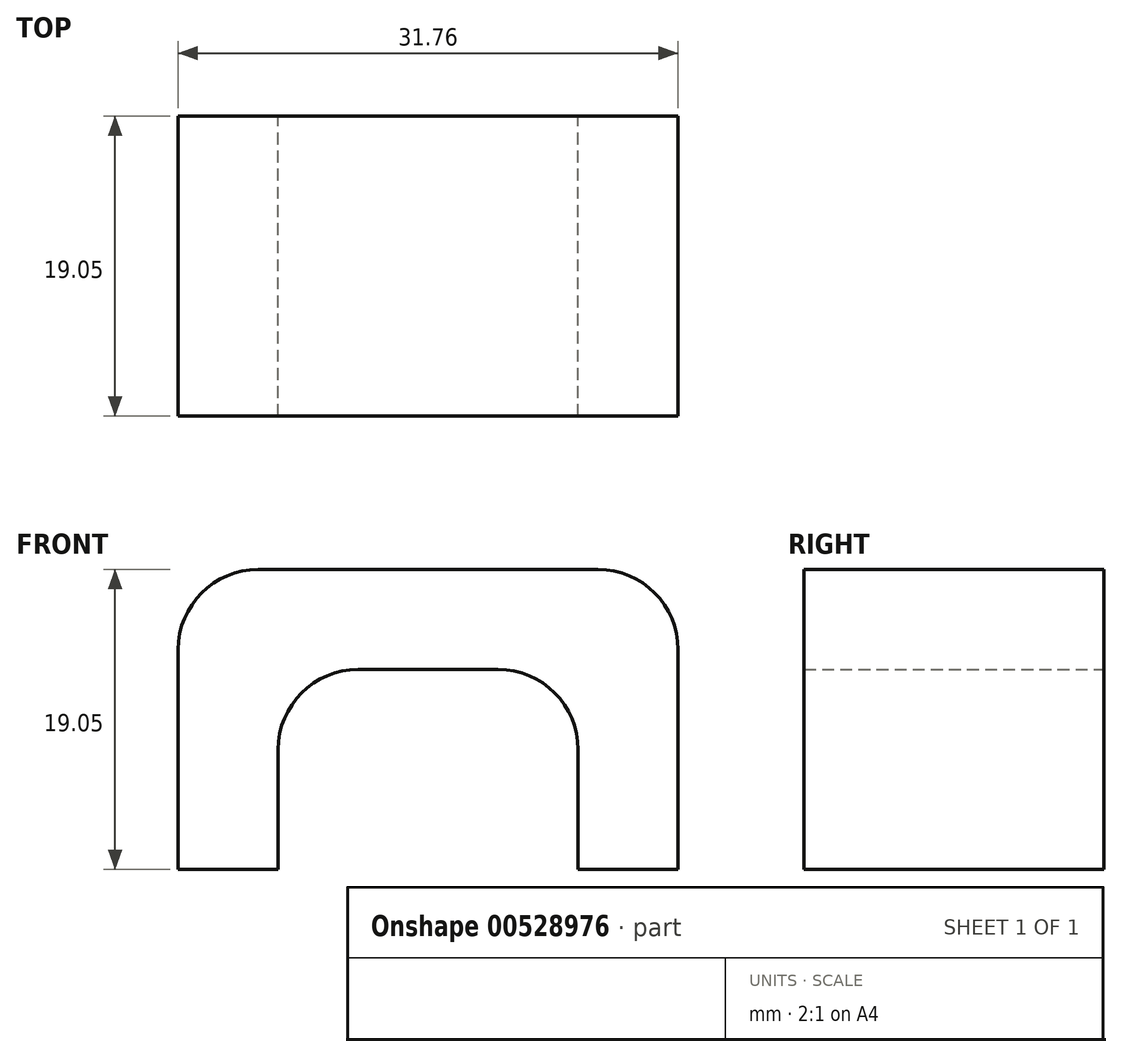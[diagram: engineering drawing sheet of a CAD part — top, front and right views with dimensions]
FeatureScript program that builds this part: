
annotation { "Feature Type Name" : "Feature", "Feature Type Description" : "" }
export const myFeature = defineFeature(function(context is Context, id is Id, definition is map)
    precondition{}
    {
        {
            var Q0;
            Q0=qCreatedBy(makeId("Front.planeOp"),FACE);
            var sketch = newSketch(context, id + "F0", { "sketchPlane" : qUnion([Q0])});
            skLineSegment(sketch, "E0", {"start": v(0, 0) * mm, "end": v(-15.87, 0) * mm});
            skLineSegment(sketch, "E1", {"start": v(-15.87, 0) * mm, "end": v(-15.87, -19.05) * mm});
            skLineSegment(sketch, "E2", {"start": v(-15.87, -19.05) * mm, "end": v(-9.52, -19.05) * mm});
            skLineSegment(sketch, "E3", {"start": v(-9.52, -19.05) * mm, "end": v(-9.52, -6.35) * mm});
            skLineSegment(sketch, "E4", {"start": v(-9.52, -6.35) * mm, "end": v(0, -6.35) * mm});
            skLineSegment(sketch, "E5", {"start": v(0, -6.35) * mm, "end": v(0, 0) * mm, "construction": true});
            skLineSegment(sketch, "E6.MirrorCS", {"start": v(15.88, 0) * mm, "end": v(15.88, -19.05) * mm});
            skLineSegment(sketch, "E7.MirrorCS", {"start": v(15.87, -19.05) * mm, "end": v(9.52, -19.05) * mm});
            skLineSegment(sketch, "E8.MirrorCS", {"start": v(9.52, -19.05) * mm, "end": v(9.52, -6.35) * mm});
            skLineSegment(sketch, "E9.MirrorCS", {"start": v(0, 0) * mm, "end": v(15.87, 0) * mm});
            skLineSegment(sketch, "E10.MirrorCS", {"start": v(9.52, -6.35) * mm, "end": v(0, -6.35) * mm});
            skSolve(sketch);
        }
        {
            var Q0;
            Q0=qSketchRegion(id+"F0",true);
            extrude(context, id + "F1", {"entities" : qUnion([Q0]), "depth" : 19.05 * mm});
        }
        {
            var Q0;
            Q0=makeQuery(id+"F1.opExtrude","SWEPT_EDGE",EDGE,{"disambiguationData":[OSD([sQuery(id+"F0.wireOp",EDGE,"E0"),sQuery(id+"F0.wireOp",EDGE,"E1")])]});
            var Q1;
            Q1=makeQuery(id+"F1.opExtrude","SWEPT_EDGE",EDGE,{"disambiguationData":[OSD([sQuery(id+"F0.wireOp",EDGE,"E3"),sQuery(id+"F0.wireOp",EDGE,"E4")])]});
            var Q2;
            Q2=makeQuery(id+"F1.opExtrude","SWEPT_EDGE",EDGE,{"disambiguationData":[OSD([sQuery(id+"F0.wireOp",EDGE,"E8.MirrorCS"),sQuery(id+"F0.wireOp",EDGE,"E10.MirrorCS")])]});
            var Q3;
            Q3=makeQuery(id+"F1.opExtrude","SWEPT_EDGE",EDGE,{"disambiguationData":[OSD([sQuery(id+"F0.wireOp",EDGE,"E6.MirrorCS"),sQuery(id+"F0.wireOp",EDGE,"E9.MirrorCS")])]});
            fillet(context, id + "F2", {"entities" : qUnion([Q0, Q1, Q2, Q3]), "radius" : 5.08 * mm, "tangentPropagation" : true, "allowEdgeOverflow" : false});
        }
    });
